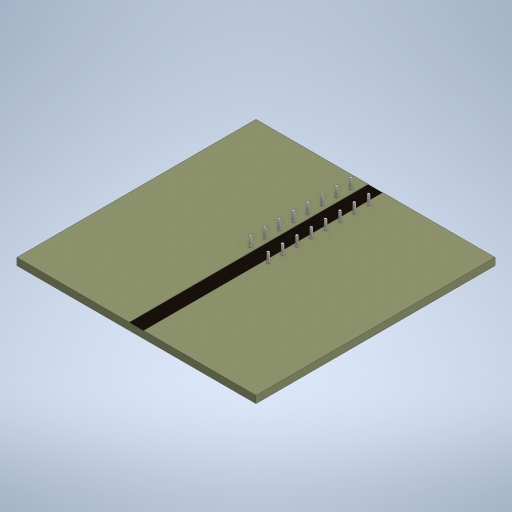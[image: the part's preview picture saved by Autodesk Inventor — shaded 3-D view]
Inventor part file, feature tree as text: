
AUTODESK INVENTOR PART (.ipt)
format: ipt  version: 2023 (Build 270158000, 158)  size: 296,448 bytes
history: native  units: in
note: dims shown in document units (in); Inventor stores cm internally (conversion verified against a paired STEP export)
features: extrude x3, sketch x3, pattern_linear x1, projected_geometry x1
ambient origin geometry x8: Origin, YZ Plane, XZ Plane, XY Plane, X Axis, Y Axis, Z Axis, Center Point
bodies: Solid1 (feature_tree)
feature tree (8):
  extrude  "Extrusion1"  Depth=3937.0079in
  extrude  "Extrusion2"  Depth=236.2205in
  extrude  "Extrusion3"  Depth=236.2205in
  pattern_linear  "Rectangular Pattern1"  Count1=100 Spacing1=0.0in
  sketch  "Sketch1"  dims[d0=3937.0079in d1=3937.0079in]
  sketch  "Sketch2"  dims[d2=118.1102in d3=0.0in d4=236.2205in]
  sketch  "Sketch3"  dims[d5=3.937in d6=0.0in d7=39.3701in d8=39.3701in d9=157.4803in d10=0.0in d11=3.1496in d13=236.2205in]
  projected_geometry  "Projected Loop1"
